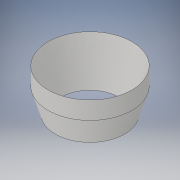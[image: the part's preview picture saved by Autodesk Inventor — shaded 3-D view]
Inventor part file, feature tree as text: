
AUTODESK INVENTOR PART (.ipt)
format: ipt  version: 2017 (Build 210142000, 142)  size: 114,176 bytes
history: native  units: in
note: dims shown in document units (in); Inventor stores cm internally (conversion verified against a paired STEP export)
features: revolve x1, sketch x1
ambient origin geometry x8: Origin, YZ Plane, XZ Plane, XY Plane, X Axis, Y Axis, Z Axis, Center Point
bodies: Solid1 (feature_tree)
feature tree (2):
  revolve  "Revolution1"  [1 undecoded]
  sketch  "Sketch1"  dims[d4=90.0deg d15=0.1024in d16=0.0846in d17=0.1024in d18=0.0433in d19=0.1147in]
note: 1 required parameter value undecoded (feature->parameter linkage not recoverable at this tier; creation-order binding heuristic only, values carry confidence <= 0.55)
